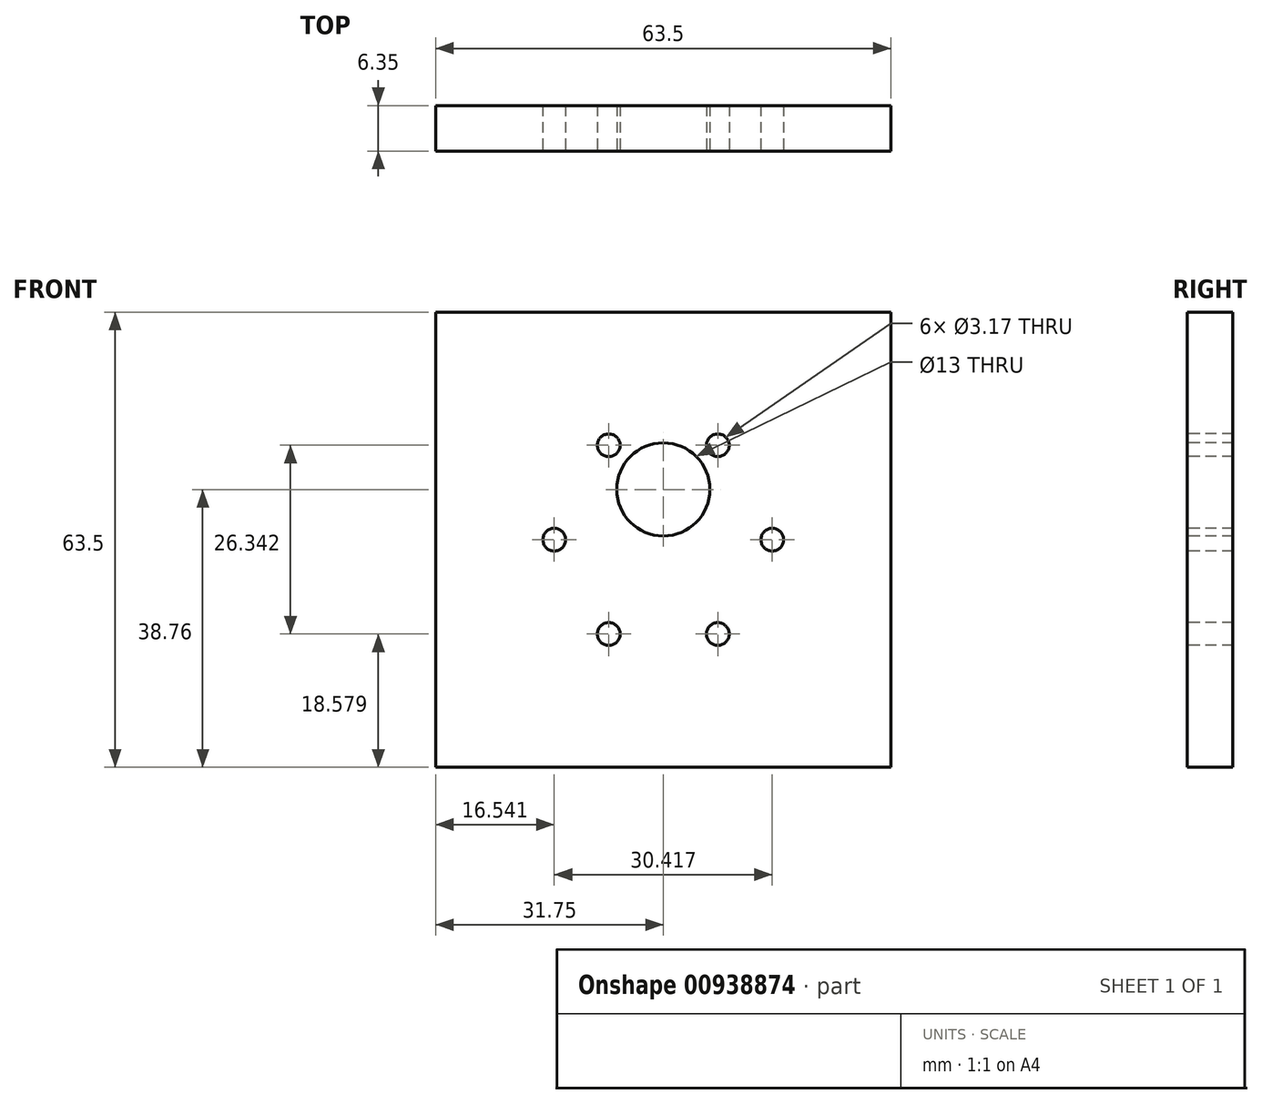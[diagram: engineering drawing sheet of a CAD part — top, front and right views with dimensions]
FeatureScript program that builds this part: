
annotation { "Feature Type Name" : "Feature", "Feature Type Description" : "" }
export const myFeature = defineFeature(function(context is Context, id is Id, definition is map)
    precondition{}
    {
        {
            var Q0;
            Q0=qCreatedBy(makeId("Front.planeOp"),FACE);
            var sketch = newSketch(context, id + "F0", { "sketchPlane" : qUnion([Q0])});
            skLineSegment(sketch, "E0.bottom", {"start": v(-31.75, 31.75) * mm, "end": v(31.75, 31.75) * mm});
            skLineSegment(sketch, "E0.top", {"start": v(-31.75, -31.75) * mm, "end": v(31.75, -31.75) * mm});
            skLineSegment(sketch, "E0.left", {"start": v(-31.75, 31.75) * mm, "end": v(-31.75, -31.75) * mm});
            skLineSegment(sketch, "E0.right", {"start": v(31.75, 31.75) * mm, "end": v(31.75, -31.75) * mm});
            skPoint(sketch, "E0.middle", {"position": v(0, 0) * mm});
            skSolve(sketch);
        }
        {
            var Q0;
            Q0=makeQuery(id+"F0.imprint","IMPRINT",FACE,{"disambiguationData":[TD([[makeQuery(id+"F0.imprint","IMPRINT",EDGE,{"derivedFrom":sQuery(id+"F0.wireOp",EDGE,"E0.bottom")}),-1.0]])]});
            extrude(context, id + "F1", {"entities" : qUnion([Q0]), "depth" : 6.35 * mm, "offsetDistance" : 25.4 * mm});
        }
        {
            var Q0;
            Q0=makeQuery(id+"F1.opExtrude","CAP_FACE",FACE,{"disambiguationData":[OSD([sQuery(id+"F0.wireOp",EDGE,"E0.bottom"),sQuery(id+"F0.wireOp",EDGE,"E0.top"),sQuery(id+"F0.wireOp",EDGE,"E0.left"),sQuery(id+"F0.wireOp",EDGE,"E0.right")])],"isStart":false});
            var sketch = newSketch(context, id + "F2", { "sketchPlane" : qUnion([Q0])});
            skCircle(sketch, "E1", {"center": v(15.2, 0) * mm, "radius": 1.59 * mm});
            skPoint(sketch, "E2.center", {"position": v(0, 0) * mm});
            skLineSegment(sketch, "E2.anchor1", {"start": v(0, 0) * mm, "end": v(15.2, 0) * mm, "construction": true});
            skLineSegment(sketch, "E2.anchor2", {"start": v(0, 0) * mm, "end": v(15.2, 0) * mm, "construction": true});
            skCircle(sketch, "E3.1.0", {"center": v(7.6, 13.17) * mm, "radius": 1.59 * mm});
            skCircle(sketch, "E3.2.0", {"center": v(-7.6, 13.17) * mm, "radius": 1.59 * mm});
            skCircle(sketch, "E3.3.0", {"center": v(-15.2, 0) * mm, "radius": 1.59 * mm});
            skCircle(sketch, "E3.4.0", {"center": v(-7.6, -13.17) * mm, "radius": 1.59 * mm});
            skCircle(sketch, "E3.5.0", {"center": v(7.6, -13.17) * mm, "radius": 1.59 * mm});
            skSolve(sketch);
        }
        {
            var Q0;
            Q0=makeQuery(id+"F2.imprint","IMPRINT",FACE,{"disambiguationData":[TD([[makeQuery(id+"F2.imprint","IMPRINT",EDGE,{"derivedFrom":sQuery(id+"F2.wireOp",EDGE,"E1")}),-1.0]])]});
            var sketch = newSketch(context, id + "F3", { "sketchPlane" : qUnion([Q0])});
            skCircle(sketch, "E4", {"center": v(0, 7.01) * mm, "radius": 6.5 * mm});
            skSolve(sketch);
        }
        {
            var Q0;
            Q0=makeQuery(id+"F2.imprint","IMPRINT",FACE,{"disambiguationData":[TD([[makeQuery(id+"F2.imprint","IMPRINT",EDGE,{"derivedFrom":sQuery(id+"F2.wireOp",EDGE,"E3.1.0")}),1.0]])]});
            var Q1;
            Q1=makeQuery(id+"F2.imprint","IMPRINT",FACE,{"disambiguationData":[TD([[makeQuery(id+"F2.imprint","IMPRINT",EDGE,{"derivedFrom":sQuery(id+"F2.wireOp",EDGE,"E1")}),1.0]])]});
            var Q2;
            Q2=makeQuery(id+"F2.imprint","IMPRINT",FACE,{"disambiguationData":[TD([[makeQuery(id+"F2.imprint","IMPRINT",EDGE,{"derivedFrom":sQuery(id+"F2.wireOp",EDGE,"E3.5.0")}),1.0]])]});
            var Q3;
            Q3=makeQuery(id+"F2.imprint","IMPRINT",FACE,{"disambiguationData":[TD([[makeQuery(id+"F2.imprint","IMPRINT",EDGE,{"derivedFrom":sQuery(id+"F2.wireOp",EDGE,"E3.4.0")}),1.0]])]});
            var Q4;
            Q4=makeQuery(id+"F2.imprint","IMPRINT",FACE,{"disambiguationData":[TD([[makeQuery(id+"F2.imprint","IMPRINT",EDGE,{"derivedFrom":sQuery(id+"F2.wireOp",EDGE,"E3.3.0")}),1.0]])]});
            var Q5;
            Q5=makeQuery(id+"F2.imprint","IMPRINT",FACE,{"disambiguationData":[TD([[makeQuery(id+"F2.imprint","IMPRINT",EDGE,{"derivedFrom":sQuery(id+"F2.wireOp",EDGE,"E3.2.0")}),1.0]])]});
            var Q6;
            Q6 = qSketchRegion(id + "F3", true);
            extrude(context, id + "F4", {"entities" : qUnion([Q0, Q1, Q2, Q3, Q4, Q5, Q6]), "operationType" : NewBodyOperationType.REMOVE, "endBound" : BoundingType.THROUGH_ALL, "oppositeDirection" : true, "depth" : 25.4 * mm, "offsetDistance" : 25.4 * mm});
        }
    });
